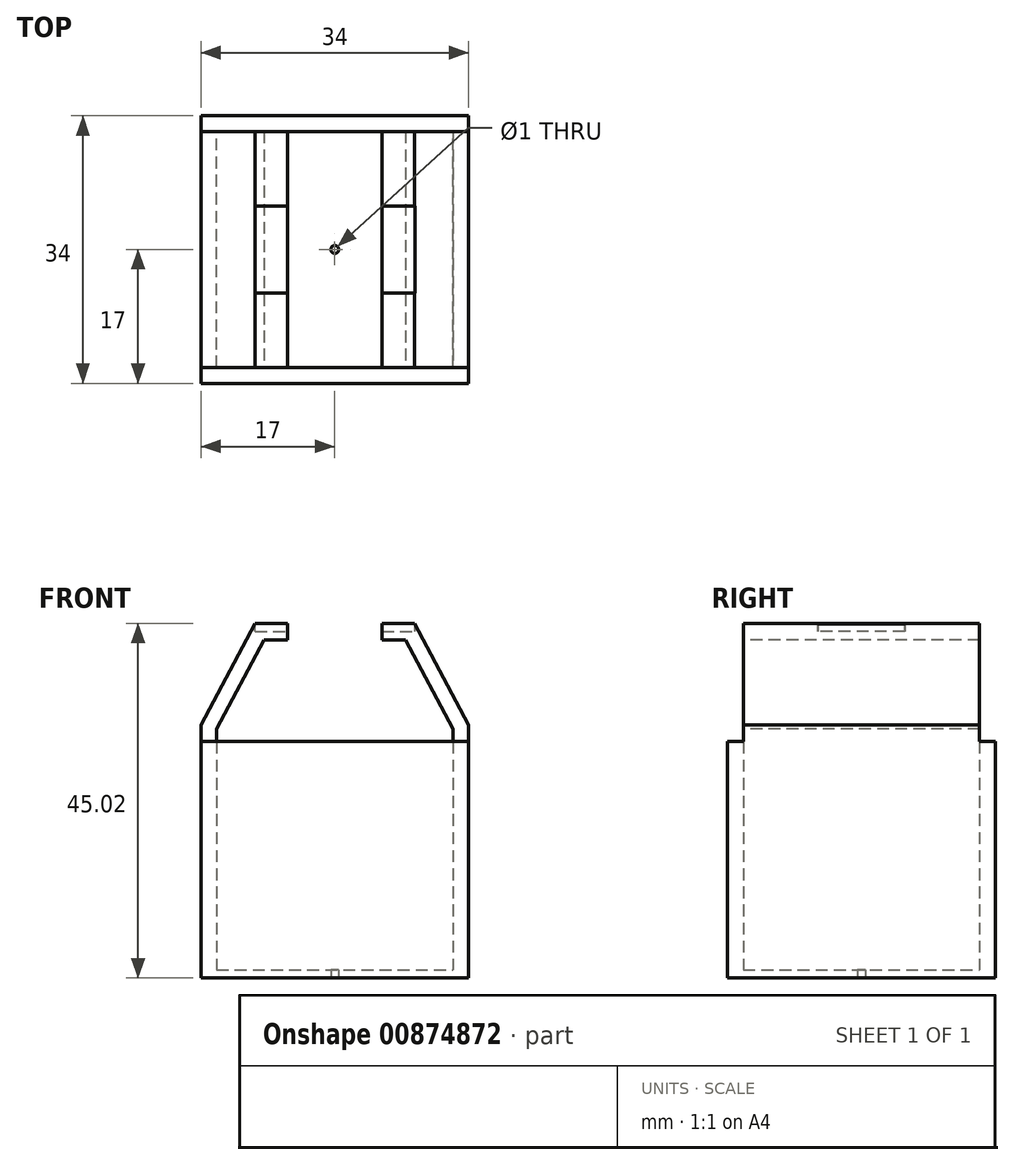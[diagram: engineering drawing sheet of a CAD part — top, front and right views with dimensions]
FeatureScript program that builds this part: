
annotation { "Feature Type Name" : "Feature", "Feature Type Description" : "" }
export const myFeature = defineFeature(function(context is Context, id is Id, definition is map)
    precondition{}
    {
        {
            var Q0;
            Q0=qCreatedBy(makeId("Top.planeOp"),FACE);
            var sketch = newSketch(context, id + "F0", { "sketchPlane" : qUnion([Q0])});
            skLineSegment(sketch, "E0.bottom", {"start": v(0, 0) * mm, "end": v(30, 0) * mm});
            skLineSegment(sketch, "E0.top", {"start": v(0, 30) * mm, "end": v(30, 30) * mm});
            skLineSegment(sketch, "E0.left", {"start": v(0, 0) * mm, "end": v(0, 30) * mm});
            skLineSegment(sketch, "E0.right", {"start": v(30, 0) * mm, "end": v(30, 30) * mm});
            skLineSegment(sketch, "E1.0", {"start": v(-2, 32) * mm, "end": v(32, 32) * mm});
            skLineSegment(sketch, "E1.1", {"start": v(-2, -2) * mm, "end": v(-2, 32) * mm});
            skLineSegment(sketch, "E1.2", {"start": v(-2, -2) * mm, "end": v(32, -2) * mm});
            skLineSegment(sketch, "E1.3", {"start": v(32, -2) * mm, "end": v(32, 32) * mm});
            skSolve(sketch);
        }
        {
            var Q0;
            Q0=makeQuery(id+"F0.imprint","IMPRINT",FACE,{"disambiguationData":[TD([[makeQuery(id+"F0.imprint","IMPRINT",EDGE,{"derivedFrom":sQuery(id+"F0.wireOp",EDGE,"E0.bottom")}),-1.0]])]});
            extrude(context, id + "F1", {"entities" : qUnion([Q0]), "depth" : 30 * mm, "offsetDistance" : 25 * mm});
        }
        {
            var Q0;
            Q0=qCreatedBy(makeId("Top.planeOp"),FACE);
            var sketch = newSketch(context, id + "F2", { "sketchPlane" : qUnion([Q0])});
            skLineSegment(sketch, "E2.bottom", {"start": v(-1.17, -1.1) * mm, "end": v(31.24, -1.1) * mm});
            skLineSegment(sketch, "E2.top", {"start": v(-1.17, 30.98) * mm, "end": v(31.24, 30.98) * mm});
            skLineSegment(sketch, "E2.left", {"start": v(-1.17, -1.1) * mm, "end": v(-1.17, 30.98) * mm});
            skLineSegment(sketch, "E2.right", {"start": v(31.24, -1.1) * mm, "end": v(31.24, 30.98) * mm});
            skSolve(sketch);
        }
        {
            var Q0;
            Q0 = qSketchRegion(id + "F2", true);
            extrude(context, id + "F3", {"entities" : qUnion([Q0]), "operationType" : NewBodyOperationType.ADD, "depth" : 1 * mm, "offsetDistance" : 25 * mm});
        }
        {
            var Q0;
            Q0=qCreatedBy(makeId("Top.planeOp"),FACE);
            var sketch = newSketch(context, id + "F4", { "sketchPlane" : qUnion([Q0])});
            skCircle(sketch, "E3", {"center": v(15, 15) * mm, "radius": 0.5 * mm});
            skSolve(sketch);
        }
        {
            var Q0;
            Q0 = qSketchRegion(id + "F4", true);
            extrude(context, id + "F5", {"entities" : qUnion([Q0]), "operationType" : NewBodyOperationType.REMOVE, "depth" : 2 * mm, "offsetDistance" : 25 * mm});
        }
        {
            var Q0;
            Q0=qCreatedBy(makeId("Front.planeOp"),FACE);
            var sketch = newSketch(context, id + "F6", { "sketchPlane" : qUnion([Q0])});
            skLineSegment(sketch, "E4.bottom", {"start": v(-2, 30) * mm, "end": v(-0.87, 30) * mm});
            skLineSegment(sketch, "E4.top", {"start": v(4.87, 45.02) * mm, "end": v(6, 45.02) * mm});
            skLineSegment(sketch, "E4.left", {"start": v(-2, 30) * mm, "end": v(-2, 32.13) * mm});
            skLineSegment(sketch, "E5.0", {"start": v(0, 31.62) * mm, "end": v(6, 42.89) * mm});
            skLineSegment(sketch, "E6.0", {"start": v(-2, 32.13) * mm, "end": v(4.87, 45.02) * mm});
            skLineSegment(sketch, "E7.MirrorCS", {"start": v(25.13, 45.02) * mm, "end": v(24, 45.02) * mm});
            skLineSegment(sketch, "E8.MirrorCS", {"start": v(32, 30) * mm, "end": v(30.87, 30) * mm});
            skLineSegment(sketch, "E9.MirrorCS", {"start": v(32, 30) * mm, "end": v(32, 32.13) * mm});
            skLineSegment(sketch, "E10.MirrorCS", {"start": v(32, 32.13) * mm, "end": v(25.13, 45.02) * mm});
            skLineSegment(sketch, "E11.MirrorCS", {"start": v(30, 31.62) * mm, "end": v(24, 42.89) * mm});
            skLineSegment(sketch, "E12", {"start": v(4.87, 45.02) * mm, "end": v(7.5, 45.02) * mm});
            skLineSegment(sketch, "E13.trimOffspring", {"start": v(22.5, 45.02) * mm, "end": v(25.13, 45.02) * mm});
            skLineSegment(sketch, "E14.trimOffspring", {"start": v(22.5, 42.89) * mm, "end": v(24, 42.89) * mm});
            skPoint(sketch, "E15.start.orphan", {"position": v(15, 42.89) * mm});
            skLineSegment(sketch, "E16", {"start": v(6, 42.89) * mm, "end": v(7.5, 42.89) * mm});
            skLineSegment(sketch, "E17", {"start": v(-2, 30) * mm, "end": v(0, 30) * mm});
            skLineSegment(sketch, "E18", {"start": v(0, 30) * mm, "end": v(0, 31.62) * mm});
            skLineSegment(sketch, "E19", {"start": v(32, 30) * mm, "end": v(30, 30) * mm});
            skLineSegment(sketch, "E20", {"start": v(30, 30) * mm, "end": v(30, 31.62) * mm});
            skLineSegment(sketch, "E21.0", {"start": v(9, 42.89) * mm, "end": v(9, 45.02) * mm});
            skLineSegment(sketch, "E22.0", {"start": v(21, 42.89) * mm, "end": v(21, 45.02) * mm});
            skLineSegment(sketch, "E23", {"start": v(7.5, 42.89) * mm, "end": v(9, 42.89) * mm});
            skLineSegment(sketch, "E24", {"start": v(7.5, 45.02) * mm, "end": v(9, 45.02) * mm});
            skLineSegment(sketch, "E25", {"start": v(21, 45.02) * mm, "end": v(22.5, 45.02) * mm});
            skLineSegment(sketch, "E26", {"start": v(21, 42.89) * mm, "end": v(22.5, 42.89) * mm});
            skSolve(sketch);
        }
        {
            var Q0;
            Q0 = qSketchRegion(id + "F6", true);
            extrude(context, id + "F7", {"entities" : qUnion([Q0]), "operationType" : NewBodyOperationType.ADD, "oppositeDirection" : true, "depth" : 30 * mm, "offsetDistance" : 25 * mm});
        }
        {
            var Q0;
            Q0=qCreatedBy(makeId("Top.planeOp"),FACE);
            cPlane(context, id + "F8", {"entities" : qUnion([Q0]), "cplaneType" : CPlaneType.OFFSET, "offset" : 46 * mm, "width" : 150 * mm, "height" : 150 * mm});
        }
        {
            var Q0;
            Q0=qCreatedBy(id+"F8.planeOp",FACE);
            var sketch = newSketch(context, id + "F9", { "sketchPlane" : qUnion([Q0])});
            skLineSegment(sketch, "E27.bottom", {"start": v(4.87, 20.5) * mm, "end": v(25.17, 20.5) * mm});
            skLineSegment(sketch, "E27.top", {"start": v(4.87, 9.5) * mm, "end": v(25.17, 9.5) * mm});
            skLineSegment(sketch, "E27.left", {"start": v(4.87, 20.5) * mm, "end": v(4.87, 9.5) * mm});
            skLineSegment(sketch, "E27.right", {"start": v(25.17, 20.5) * mm, "end": v(25.17, 9.5) * mm});
            skLineSegment(sketch, "E28", {"start": v(4.87, 15) * mm, "end": v(12.31, 15) * mm});
            skSolve(sketch);
        }
        {
            var Q0;
            Q0 = qSketchRegion(id + "F9", true);
            extrude(context, id + "F10", {"entities" : qUnion([Q0]), "operationType" : NewBodyOperationType.REMOVE, "oppositeDirection" : true, "depth" : 2 * mm, "offsetDistance" : 25 * mm});
        }
    });
